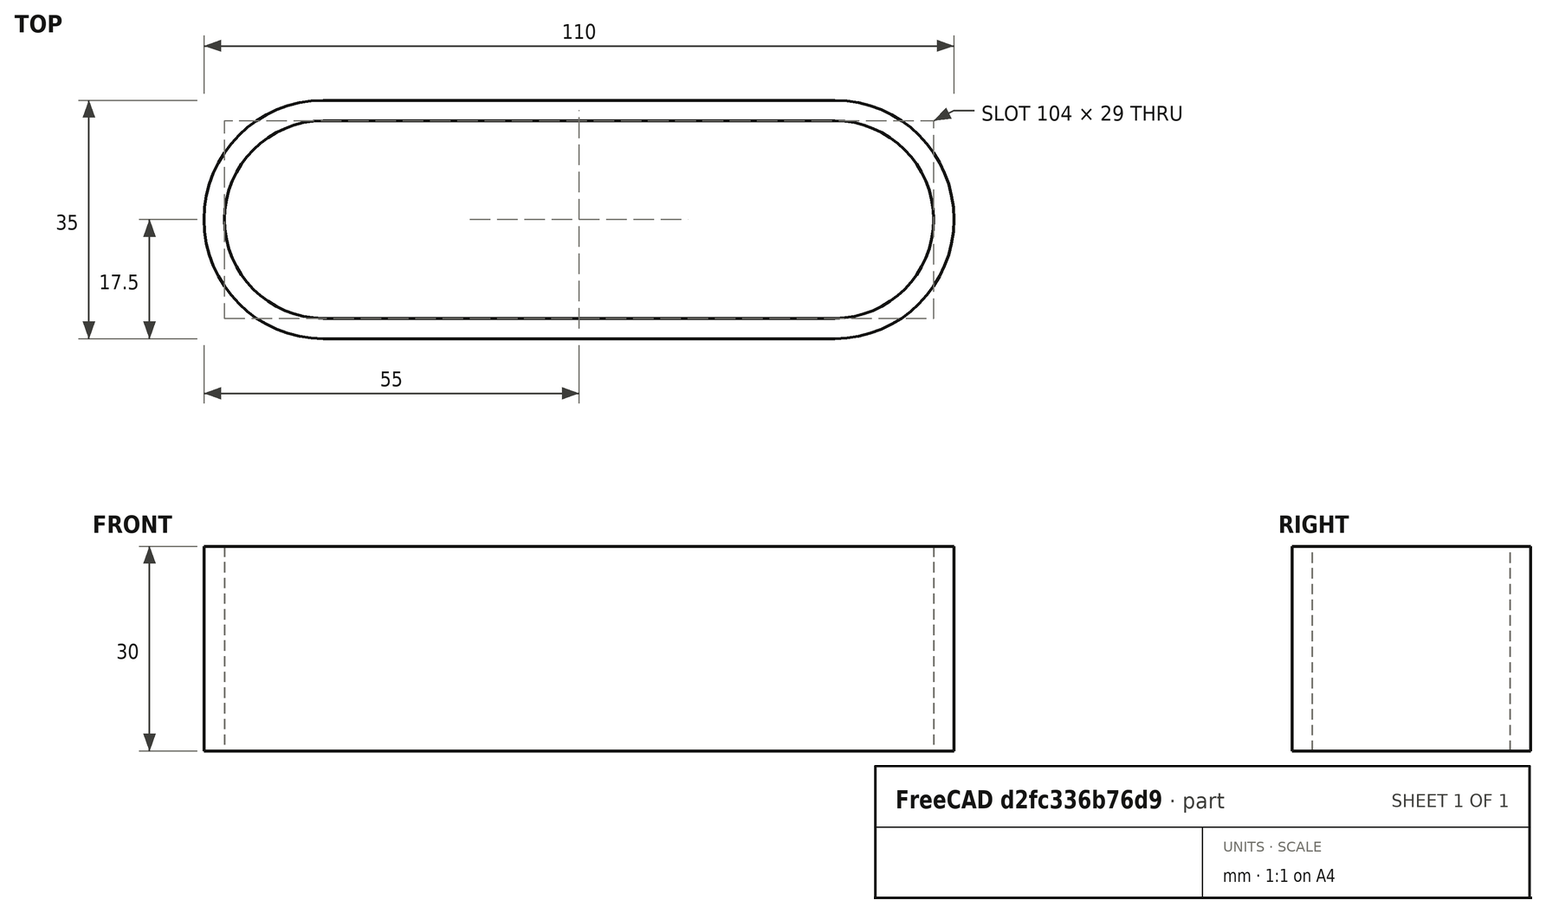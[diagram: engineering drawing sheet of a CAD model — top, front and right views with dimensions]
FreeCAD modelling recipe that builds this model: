
FCSTD DOCUMENT  (FreeCAD 0.18.3R)
Label: tutorial4
License: All rights reserved
LicenseURL: http://en.wikipedia.org/wiki/All_rights_reserved
objects: Sketcher::SketchObject×1, PartDesign::Pad×1, PartDesign::Body×1
note: 4 computed .brp shape members not serialized (recipe doc carries the construction recipe); baked Part::Feature solids carry a one-line shape summary decoded from their .brp

FEATURE [Sketcher::SketchObject] Sketch
  MapMode = 5
  Support = -> [XY_Plane]
  sketch-geometry (8):
    g0: ArcOfCircle CenterX=0 CenterY=17.5 CenterZ=0 NormalX=0 NormalY=0 NormalZ=1 AngleXU=0 Radius=14.5 StartAngle=1.5708 EndAngle=4.71239
    g1: ArcOfCircle CenterX=75 CenterY=17.5 CenterZ=0 NormalX=0 NormalY=0 NormalZ=1 AngleXU=0 Radius=14.5 StartAngle=4.71239 EndAngle=7.85398
    g2: LineSegment StartX=0 StartY=3 StartZ=0 EndX=75 EndY=3 EndZ=0
    g3: LineSegment StartX=-1.8e-15 StartY=32 StartZ=0 EndX=75 EndY=32 EndZ=0
    g4: ArcOfCircle CenterX=0 CenterY=17.5 CenterZ=0 NormalX=0 NormalY=0 NormalZ=1 AngleXU=0 Radius=17.5 StartAngle=1.5708 EndAngle=4.71239
    g5: ArcOfCircle CenterX=75 CenterY=17.5 CenterZ=0 NormalX=0 NormalY=0 NormalZ=1 AngleXU=0 Radius=17.5 StartAngle=4.71239 EndAngle=7.85398
    g6: LineSegment StartX=-3.2e-15 StartY=0 StartZ=0 EndX=75 EndY=0 EndZ=0
    g7: LineSegment StartX=-2.2e-15 StartY=35 StartZ=0 EndX=75 EndY=35 EndZ=0
  constraints (17):
    c: Tangent(g0,g3) = 1.5708
    c: Tangent(g0,g2) = -1.5708
    c: Tangent(g2,g1) = -1.5708
    c: Tangent(g3,g1) = 1.5708
    c: Horizontal(g2)
    c: Equal(g0,g1)
    c: DistanceX(g3,g3) = 75
    c: DistanceY(g0,g0) = 29
    c: Tangent(g4,g7) = 1.5708
    c: Tangent(g4,g6) = -1.5708
    c: Tangent(g6,g5) = -1.5708
    c: Tangent(g7,g5) = 1.5708
    c: Horizontal(g6)
    c: Coincident(g4,g0)
    c: Coincident(g5,g1)
    c: DistanceY(g5,g1) = 3
    c: Coincident(g4,g-1)
FEATURE [PartDesign::Pad] Pad
  Length = 30
  Length2 = 100
  Profile = -> Sketch
  Refine = true
  Type = 0
FEATURE [PartDesign::Body] Body
  Group = -> [Sketch,Pad]
  Origin = -> Origin
  Tip = -> Pad
